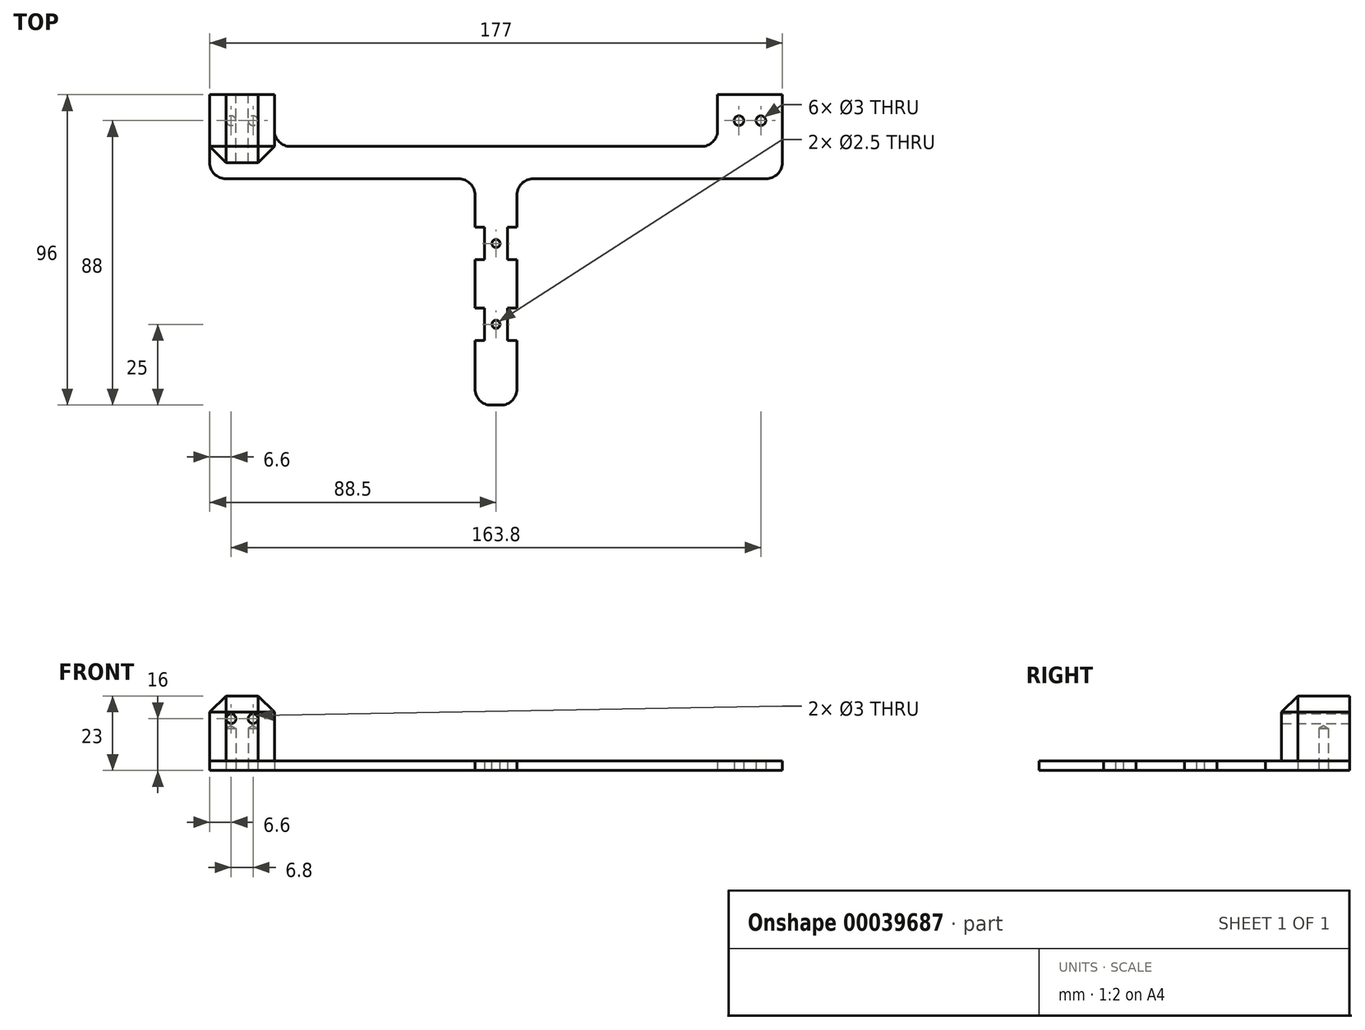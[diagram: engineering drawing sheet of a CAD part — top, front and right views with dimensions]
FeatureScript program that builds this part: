
annotation { "Feature Type Name" : "Feature", "Feature Type Description" : "" }
export const myFeature = defineFeature(function(context is Context, id is Id, definition is map)
    precondition{}
    {
        {
            var Q0;
            Q0=qCreatedBy(makeId("Top.planeOp"),FACE);
            var sketch = newSketch(context, id + "F0", { "sketchPlane" : qUnion([Q0])});
            skLineSegment(sketch, "E0", {"start": v(-6.5, -80) * mm, "end": v(0, -80) * mm});
            skLineSegment(sketch, "E1", {"start": v(0, 0) * mm, "end": v(-68.5, 0) * mm});
            skLineSegment(sketch, "E2", {"start": v(-68.5, 0) * mm, "end": v(-68.5, 16) * mm});
            skLineSegment(sketch, "E3", {"start": v(-68.5, 16) * mm, "end": v(-88.5, 16) * mm});
            skLineSegment(sketch, "E4", {"start": v(-88.5, 16) * mm, "end": v(-88.5, -10) * mm});
            skLineSegment(sketch, "E5", {"start": v(-88.5, -10) * mm, "end": v(-6.5, -10) * mm});
            skLineSegment(sketch, "E6", {"start": v(-6.5, -10) * mm, "end": v(-6.5, -25) * mm});
            skLineSegment(sketch, "E7", {"start": v(0, -80) * mm, "end": v(0, 0) * mm});
            skLineSegment(sketch, "E8", {"start": v(-6.5, -25) * mm, "end": v(-3.5, -25) * mm});
            skLineSegment(sketch, "E9", {"start": v(-3.5, -25) * mm, "end": v(-3.5, -35) * mm});
            skLineSegment(sketch, "E10", {"start": v(-3.5, -35) * mm, "end": v(-6.5, -35) * mm});
            skLineSegment(sketch, "E11.trimOffspring", {"start": v(-6.5, -35) * mm, "end": v(-6.5, -50) * mm});
            skLineSegment(sketch, "E12", {"start": v(-6.5, -60) * mm, "end": v(-3.5, -60) * mm});
            skLineSegment(sketch, "E13", {"start": v(-3.5, -60) * mm, "end": v(-3.5, -50) * mm});
            skLineSegment(sketch, "E14", {"start": v(-3.5, -50) * mm, "end": v(-6.5, -50) * mm});
            skLineSegment(sketch, "E15.trimOffspring", {"start": v(-6.5, -60) * mm, "end": v(-6.5, -80) * mm});
            skPoint(sketch, "E16", {"position": v(-81.9, 8) * mm});
            skPoint(sketch, "E17", {"position": v(-75.1, 8) * mm});
            skSolve(sketch);
        }
        {
            var Q0;
            Q0=makeQuery(id+"F0.imprint","IMPRINT",FACE,{"disambiguationData":[TD([[makeQuery(id+"F0.imprint","IMPRINT",EDGE,{"derivedFrom":sQuery(id+"F0.wireOp",EDGE,"E0")}),1.0]])]});
            extrude(context, id + "F1", {"entities" : qUnion([Q0]), "depth" : 3 * mm});
        }
        {
            var Q0;
            Q0=sQuery(id+"F0.wireOp",VERTEX,"E16");
            var Q1;
            Q1=sQuery(id+"F0.wireOp",VERTEX,"E17");
            var Q2;
            Q2=makeQuery(id+"F1.opExtrude","SWEPT_BODY",BODY,{"disambiguationData":[OSD([sQuery(id+"F0.wireOp",EDGE,"E0"),sQuery(id+"F0.wireOp",EDGE,"E1"),sQuery(id+"F0.wireOp",EDGE,"E2"),sQuery(id+"F0.wireOp",EDGE,"E3"),sQuery(id+"F0.wireOp",EDGE,"E4"),sQuery(id+"F0.wireOp",EDGE,"E5"),sQuery(id+"F0.wireOp",EDGE,"E6"),sQuery(id+"F0.wireOp",EDGE,"E7"),sQuery(id+"F0.wireOp",EDGE,"E8"),sQuery(id+"F0.wireOp",EDGE,"E9"),sQuery(id+"F0.wireOp",EDGE,"E10"),sQuery(id+"F0.wireOp",EDGE,"E11.trimOffspring"),sQuery(id+"F0.wireOp",EDGE,"E12"),sQuery(id+"F0.wireOp",EDGE,"E13"),sQuery(id+"F0.wireOp",EDGE,"E14"),sQuery(id+"F0.wireOp",EDGE,"E15.trimOffspring")])]});
            var Q3;
            Q3=makeQuery(id+"F9.opExtrude","SWEPT_BODY",BODY,{"disambiguationData":[OSD([sQuery(id+"F8.wireOp",EDGE,"E23.bottom"),sQuery(id+"F8.wireOp",EDGE,"E23.top"),sQuery(id+"F8.wireOp",EDGE,"E23.left"),sQuery(id+"F8.wireOp",EDGE,"E23.right")])]});
            hole(context, id + "F2", {"style" : HoleStyle.SIMPLE, "holeDiameter" : 3 * mm, "endStyle" : HoleEndStyle.BLIND, "oppositeDirection" : true, "holeDepth" : 14 * mm, "locations" : qUnion([Q0, Q1]), "scope" : qUnion([Q2, Q3])});
        }
        {
            var Q0;
            Q0=makeQuery(id+"F1.opExtrude","SWEPT_FACE",FACE,{"disambiguationData":[OSD([sQuery(id+"F0.wireOp",EDGE,"E4")])]});
            cPlane(context, id + "F3", {"entities" : qUnion([Q0]), "cplaneType" : CPlaneType.OFFSET, "offset" : 0 * mm, "width" : 150 * mm, "height" : 150 * mm});
        }
        {
            var Q0;
            Q0=makeQuery(id+"F1.opExtrude","SWEPT_BODY",BODY,{"disambiguationData":[OSD([sQuery(id+"F0.wireOp",EDGE,"E0"),sQuery(id+"F0.wireOp",EDGE,"E1"),sQuery(id+"F0.wireOp",EDGE,"E2"),sQuery(id+"F0.wireOp",EDGE,"E3"),sQuery(id+"F0.wireOp",EDGE,"E4"),sQuery(id+"F0.wireOp",EDGE,"E5"),sQuery(id+"F0.wireOp",EDGE,"E6"),sQuery(id+"F0.wireOp",EDGE,"E7")])]});
            var Q1;
            Q1=qCreatedBy(makeId("Right.planeOp"),FACE);
            mirror(context, id + "F4", {"operationType" : NewBodyOperationType.ADD, "entities" : qUnion([Q0]), "mirrorPlane" : qUnion([Q1])});
        }
        {
            var Q0;
            Q0=makeQuery(id+"F1.opExtrude","SWEPT_EDGE",EDGE,{"disambiguationData":[OSD([sQuery(id+"F0.wireOp",EDGE,"E0"),sQuery(id+"F0.wireOp",EDGE,"E15.trimOffspring")])]});
            var Q1;
            Q1=makeQuery(id+"F1.opExtrude","SWEPT_EDGE",EDGE,{"disambiguationData":[OSD([sQuery(id+"F0.wireOp",EDGE,"E0"),sQuery(id+"F0.wireOp",EDGE,"E15.trimOffspring")])]});
            var Q2;
            Q2=makeQuery(id+"F1.opExtrude","SWEPT_EDGE",EDGE,{"disambiguationData":[OSD([sQuery(id+"F0.wireOp",EDGE,"E0"),sQuery(id+"F0.wireOp",EDGE,"E15.trimOffspring")])]});
            var Q3;
            Q3=makeQuery(id+"F1.opExtrude","SWEPT_EDGE",EDGE,{"disambiguationData":[OSD([sQuery(id+"F0.wireOp",EDGE,"E5"),sQuery(id+"F0.wireOp",EDGE,"E6")])]});
            var Q4;
            Q4=makeQuery(id+"F1.opExtrude","SWEPT_EDGE",EDGE,{"disambiguationData":[OSD([sQuery(id+"F0.wireOp",EDGE,"E5"),sQuery(id+"F0.wireOp",EDGE,"E6")])]});
            var Q5;
            Q5=makeQuery(id+"F1.opExtrude","SWEPT_EDGE",EDGE,{"disambiguationData":[OSD([sQuery(id+"F0.wireOp",EDGE,"E4"),sQuery(id+"F0.wireOp",EDGE,"E5")])]});
            var Q6;
            Q6=makeQuery(id+"F1.opExtrude","SWEPT_EDGE",EDGE,{"disambiguationData":[OSD([sQuery(id+"F0.wireOp",EDGE,"E1"),sQuery(id+"F0.wireOp",EDGE,"E2")])]});
            var Q7;
            Q7=makeQuery(id+"F1.opExtrude","SWEPT_EDGE",EDGE,{"disambiguationData":[OSD([sQuery(id+"F0.wireOp",EDGE,"E1"),sQuery(id+"F0.wireOp",EDGE,"E2")])]});
            var Q8;
            Q8=makeQuery(id+"F4.opPattern","COPY",EDGE,{"derivedFrom":makeQuery(id+"F1.opExtrude","SWEPT_EDGE",EDGE,{"disambiguationData":[OSD([sQuery(id+"F0.wireOp",EDGE,"E0"),sQuery(id+"F0.wireOp",EDGE,"E15.trimOffspring")])]}),"instanceName":"1"});
            var Q9;
            Q9=makeQuery(id+"F4.opPattern","COPY",EDGE,{"derivedFrom":makeQuery(id+"F1.opExtrude","SWEPT_EDGE",EDGE,{"disambiguationData":[OSD([sQuery(id+"F0.wireOp",EDGE,"E5"),sQuery(id+"F0.wireOp",EDGE,"E6")])]}),"instanceName":"1"});
            var Q10;
            Q10=makeQuery(id+"F4.opPattern","COPY",EDGE,{"derivedFrom":makeQuery(id+"F1.opExtrude","SWEPT_EDGE",EDGE,{"disambiguationData":[OSD([sQuery(id+"F0.wireOp",EDGE,"E5"),sQuery(id+"F0.wireOp",EDGE,"E6")])]}),"instanceName":"1"});
            var Q11;
            Q11=makeQuery(id+"F4.opPattern","COPY",EDGE,{"derivedFrom":makeQuery(id+"F1.opExtrude","SWEPT_EDGE",EDGE,{"disambiguationData":[OSD([sQuery(id+"F0.wireOp",EDGE,"E4"),sQuery(id+"F0.wireOp",EDGE,"E5")])]}),"instanceName":"1"});
            var Q12;
            Q12=makeQuery(id+"F4.opPattern","COPY",EDGE,{"derivedFrom":makeQuery(id+"F1.opExtrude","SWEPT_EDGE",EDGE,{"disambiguationData":[OSD([sQuery(id+"F0.wireOp",EDGE,"E1"),sQuery(id+"F0.wireOp",EDGE,"E2")])]}),"instanceName":"1"});
            var Q13;
            Q13=makeQuery(id+"Fxr2APgajM1lZgj_1.opExtrude","CAP_EDGE",EDGE,{"disambiguationData":[OSD([sQuery(id+"FLPkPK4QHD9QZg1_1.wireOp",EDGE,"44fa8a31-083d-4de4-9cf4-250411aad0ca.top")])],"isStart":true});
            var Q14;
            Q14=makeQuery(id+"Fxr2APgajM1lZgj_1.opExtrude","CAP_EDGE",EDGE,{"disambiguationData":[OSD([sQuery(id+"FLPkPK4QHD9QZg1_1.wireOp",EDGE,"44fa8a31-083d-4de4-9cf4-250411aad0ca.top")])],"isStart":false});
            var Q15;
            Q15=makeQuery(id+"F4.opPattern","COPY",EDGE,{"derivedFrom":makeQuery(id+"Fxr2APgajM1lZgj_1.opExtrude","CAP_EDGE",EDGE,{"disambiguationData":[OSD([sQuery(id+"FLPkPK4QHD9QZg1_1.wireOp",EDGE,"44fa8a31-083d-4de4-9cf4-250411aad0ca.top")])],"isStart":false}),"instanceName":"1"});
            var Q16;
            Q16=makeQuery(id+"F4.opPattern","COPY",EDGE,{"derivedFrom":makeQuery(id+"Fxr2APgajM1lZgj_1.opExtrude","CAP_EDGE",EDGE,{"disambiguationData":[OSD([sQuery(id+"FLPkPK4QHD9QZg1_1.wireOp",EDGE,"44fa8a31-083d-4de4-9cf4-250411aad0ca.top")])],"isStart":true}),"instanceName":"1"});
            fillet(context, id + "F5", {"entities" : qUnion([Q0, Q1, Q2, Q3, Q4, Q5, Q6, Q7, Q8, Q9, Q10, Q11, Q12, Q13, Q14, Q15, Q16]), "radius" : 5 * mm, "tangentPropagation" : true, "allowEdgeOverflow" : false});
        }
        {
            var Q0;
            {var subQ0=makeQuery(id+"F1.opExtrude","CAP_FACE",FACE,{"disambiguationData":[OSD([sQuery(id+"F0.wireOp",EDGE,"E0"),sQuery(id+"F0.wireOp",EDGE,"E1"),sQuery(id+"F0.wireOp",EDGE,"E2"),sQuery(id+"F0.wireOp",EDGE,"E3"),sQuery(id+"F0.wireOp",EDGE,"E4"),sQuery(id+"F0.wireOp",EDGE,"E5"),sQuery(id+"F0.wireOp",EDGE,"E6"),sQuery(id+"F0.wireOp",EDGE,"E7"),sQuery(id+"F0.wireOp",EDGE,"E8"),sQuery(id+"F0.wireOp",EDGE,"E9"),sQuery(id+"F0.wireOp",EDGE,"E10"),sQuery(id+"F0.wireOp",EDGE,"E11.trimOffspring"),sQuery(id+"F0.wireOp",EDGE,"E12"),sQuery(id+"F0.wireOp",EDGE,"E13"),sQuery(id+"F0.wireOp",EDGE,"E14"),sQuery(id+"F0.wireOp",EDGE,"E15.trimOffspring")])],"isStart":false});Q0=makeQuery(id+"F4.boolean.opBoolean","MERGE",FACE,{"derivedFrom":[subQ0,makeQuery(id+"F4.opPattern","COPY",FACE,{"derivedFrom":subQ0,"instanceName":"1"})]});}
            var sketch = newSketch(context, id + "F6", { "sketchPlane" : qUnion([Q0])});
            skLineSegment(sketch, "E18", {"start": v(-3.5, -25) * mm, "end": v(3.5, -35) * mm, "construction": true});
            skLineSegment(sketch, "E19", {"start": v(-3.5, -50) * mm, "end": v(3.5, -60) * mm, "construction": true});
            skPoint(sketch, "E20", {"position": v(0, -30) * mm});
            skPoint(sketch, "E21", {"position": v(0, -55) * mm});
            skSolve(sketch);
        }
        {
            var Q0;
            Q0=sQuery(id+"F6.wireOp",VERTEX,"E20");
            var Q1;
            Q1=sQuery(id+"F6.wireOp",VERTEX,"E21");
            var Q2;
            Q2=makeQuery(id+"F1.opExtrude","SWEPT_BODY",BODY,{"disambiguationData":[OSD([sQuery(id+"F0.wireOp",EDGE,"E0"),sQuery(id+"F0.wireOp",EDGE,"E1"),sQuery(id+"F0.wireOp",EDGE,"E2"),sQuery(id+"F0.wireOp",EDGE,"E3"),sQuery(id+"F0.wireOp",EDGE,"E4"),sQuery(id+"F0.wireOp",EDGE,"E5"),sQuery(id+"F0.wireOp",EDGE,"E6"),sQuery(id+"F0.wireOp",EDGE,"E7"),sQuery(id+"F0.wireOp",EDGE,"E8"),sQuery(id+"F0.wireOp",EDGE,"E9"),sQuery(id+"F0.wireOp",EDGE,"E10"),sQuery(id+"F0.wireOp",EDGE,"E11.trimOffspring"),sQuery(id+"F0.wireOp",EDGE,"E12"),sQuery(id+"F0.wireOp",EDGE,"E13"),sQuery(id+"F0.wireOp",EDGE,"E14"),sQuery(id+"F0.wireOp",EDGE,"E15.trimOffspring")])]});
            hole(context, id + "F7", {"style" : HoleStyle.SIMPLE, "holeDiameter" : 2.5 * mm, "endStyle" : HoleEndStyle.THROUGH, "locations" : qUnion([Q0, Q1]), "scope" : qUnion([Q2])});
        }
        {
            var Q0;
            Q0=qCreatedBy(id+"F3.planeOp",FACE);
            var sketch = newSketch(context, id + "F8", { "sketchPlane" : qUnion([Q0])});
            skPoint(sketch, "E22.2", {"position": v(5, 3) * mm});
            skLineSegment(sketch, "E23.bottom", {"start": v(5, 3) * mm, "end": v(-16, 3) * mm});
            skLineSegment(sketch, "E23.top", {"start": v(5, 23) * mm, "end": v(-16, 23) * mm});
            skLineSegment(sketch, "E23.left", {"start": v(5, 3) * mm, "end": v(5, 23) * mm});
            skLineSegment(sketch, "E23.right", {"start": v(-16, 3) * mm, "end": v(-16, 23) * mm});
            skSolve(sketch);
        }
        {
            var Q0;
            Q0=makeQuery(id+"F8.imprint","IMPRINT",FACE,{"disambiguationData":[TD([[makeQuery(id+"F8.imprint","IMPRINT",EDGE,{"derivedFrom":sQuery(id+"F8.wireOp",EDGE,"E23.bottom")}),-1.0]])]});
            var Q1;
            Q1=makeQuery(id+"Fxr2APgajM1lZgj_1.boolean.opBoolean","MERGE",FACE,{"derivedFrom":[makeQuery(id+"F1.opExtrude","SWEPT_FACE",FACE,{"disambiguationData":[OSD([sQuery(id+"F0.wireOp",EDGE,"E2")])]}),makeQuery(id+"Fxr2APgajM1lZgj_1.opExtrude","CAP_FACE",FACE,{"disambiguationData":[OSD([sQuery(id+"FLPkPK4QHD9QZg1_1.wireOp",EDGE,"44fa8a31-083d-4de4-9cf4-250411aad0ca.top"),sQuery(id+"FLPkPK4QHD9QZg1_1.wireOp",EDGE,"44fa8a31-083d-4de4-9cf4-250411aad0ca.left"),sQuery(id+"FLPkPK4QHD9QZg1_1.wireOp",EDGE,"44fa8a31-083d-4de4-9cf4-250411aad0ca.right"),sQuery(id+"FLPkPK4QHD9QZg1_1.wireOp",EDGE,"e8043008-6b7d-4488-b093-870e8edf5c2a"),sQuery(id+"FLPkPK4QHD9QZg1_1.wireOp",EDGE,"03713cbf-c19a-46bf-bc02-ad075d37f609"),sQuery(id+"FLPkPK4QHD9QZg1_1.wireOp",EDGE,"37d69354-0e40-4887-8fbb-110e2ddce90a")])],"isStart":false})]});
            extrude(context, id + "F9", {"entities" : qUnion([Q0]), "endBound" : BoundingType.UP_TO_SURFACE, "oppositeDirection" : true, "endBoundEntityFace" : qUnion([Q1]), "depth" : 25 * mm});
        }
        {
            var Q0;
            Q0=makeQuery(id+"F9.opExtrude","SWEPT_FACE",FACE,{"disambiguationData":[OSD([sQuery(id+"F8.wireOp",EDGE,"E23.right")])]});
            var sketch = newSketch(context, id + "F10", { "sketchPlane" : qUnion([Q0])});
            skPoint(sketch, "E24", {"position": v(75.1, 16) * mm});
            skPoint(sketch, "E25", {"position": v(81.9, 16) * mm});
            skSolve(sketch);
        }
        {
            var Q0;
            Q0=sQuery(id+"F10.wireOp",VERTEX,"E25");
            var Q1;
            Q1=sQuery(id+"F10.wireOp",VERTEX,"E24");
            var Q2;
            Q2=makeQuery(id+"F9.opExtrude","SWEPT_BODY",BODY,{"disambiguationData":[OSD([sQuery(id+"F8.wireOp",EDGE,"E23.bottom"),sQuery(id+"F8.wireOp",EDGE,"E23.top"),sQuery(id+"F8.wireOp",EDGE,"E23.left"),sQuery(id+"F8.wireOp",EDGE,"E23.right")])]});
            hole(context, id + "F11", {"style" : HoleStyle.SIMPLE, "holeDiameter" : 3 * mm, "endStyle" : HoleEndStyle.THROUGH, "locations" : qUnion([Q0, Q1]), "scope" : qUnion([Q2])});
        }
        {
            var Q0;
            Q0=makeQuery(id+"F9.opExtrude","SWEPT_FACE",FACE,{"disambiguationData":[OSD([sQuery(id+"F8.wireOp",EDGE,"E23.bottom")])]});
            var sketch = newSketch(context, id + "F12", { "sketchPlane" : qUnion([Q0])});
            skPoint(sketch, "E26", {"position": v(-81.9, -8) * mm});
            skPoint(sketch, "E27", {"position": v(-75.1, -8) * mm});
            skSolve(sketch);
        }
        {
            var Q0;
            Q0=makeQuery(id+"F9.opExtrude","CAP_EDGE",EDGE,{"disambiguationData":[OSD([sQuery(id+"F8.wireOp",EDGE,"E23.top")])],"isStart":true});
            var Q1;
            Q1=makeQuery(id+"F9.opExtrude","CAP_EDGE",EDGE,{"disambiguationData":[OSD([sQuery(id+"F8.wireOp",EDGE,"E23.top")])],"isStart":false});
            var Q2;
            Q2=makeQuery(id+"F9.opExtrude","CAP_EDGE",EDGE,{"disambiguationData":[OSD([sQuery(id+"F8.wireOp",EDGE,"E23.left")])],"isStart":true});
            var Q3;
            Q3=makeQuery(id+"F9.opExtrude","CAP_EDGE",EDGE,{"disambiguationData":[OSD([sQuery(id+"F8.wireOp",EDGE,"E23.left")])],"isStart":false});
            var Q4;
            Q4=makeQuery(id+"F9.opExtrude","SWEPT_EDGE",EDGE,{"disambiguationData":[OSD([sQuery(id+"F8.wireOp",EDGE,"E23.top"),sQuery(id+"F8.wireOp",EDGE,"E23.left")])]});
            chamfer(context, id + "F13", {"entities" : qUnion([Q0, Q1, Q2, Q3, Q4]), "width" : 5 * mm, "tangentPropagation" : true});
        }
        {
            var Q0;
            Q0=sQuery(id+"F12.wireOp",VERTEX,"E26");
            var Q1;
            Q1=sQuery(id+"F12.wireOp",VERTEX,"E27");
            var Q2;
            Q2=makeQuery(id+"F9.opExtrude","SWEPT_BODY",BODY,{"disambiguationData":[OSD([sQuery(id+"F8.wireOp",EDGE,"E23.bottom"),sQuery(id+"F8.wireOp",EDGE,"E23.top"),sQuery(id+"F8.wireOp",EDGE,"E23.left"),sQuery(id+"F8.wireOp",EDGE,"E23.right")])]});
            hole(context, id + "F14", {"style" : HoleStyle.SIMPLE, "holeDiameter" : 3 * mm, "endStyle" : HoleEndStyle.BLIND, "holeDepth" : 10 * mm, "locations" : qUnion([Q0, Q1]), "scope" : qUnion([Q2])});
        }
    });
